# Revit family: Good-Valvula_Arco_Escuadra_A-80
name_source: partatom
category: Pipe Accessories
units: mm (PartAtom-declared; Revit-internal decimal feet)

## family parameters
Always vertical = Yes
Cut with Voids When Loaded = No
OmniClass Number = 23.65.55.14.21
OmniClass Title = Non-Return Valves for Liquid Services
Part Type = Valve - Normal
Round Connector Dimension = Use Radius
Shared = No
Work Plane-Based = No

## types (2) — shared parameters
A = 80 mm  [stored 0.262467 ft]
Altura = 24 mm
Ancho Símbolo = 15 mm
B = 48 mm  [stored 0.15748 ft]
C = 13 mm
Description = Llave escuadra A-80
Diámetro Nominal 1 = 13 mm
K Coefficient = 0.35
Manufacturer = Vávulas Arco S.L
Material = Jatón Europeo CW617N - Chromado
Radio Nominal 1 = 6 mm
URL = www.valvulasarco.com

## per-type parameters (varying)
| type | Cost | D | Diámetro Nominal 2 | Model | Radio Nominal 2 |
| 1/2M x 3/8M | €5.80 | 10 mm  [stored 0.0328084 ft] | 10 mm | NOV76MAC | 5 mm |
| 1/2M x 1/2M | €6.20 | 13 mm | 13 mm | NOV91MAC | 6 mm |

note: [stored X ft] marks values corroborated as IEEE doubles in the binary element streams (Revit-internal decimal feet)

## geometry (parser evidence)
native form markers: Sweep x2
no freeform markers — native parametric forms only
